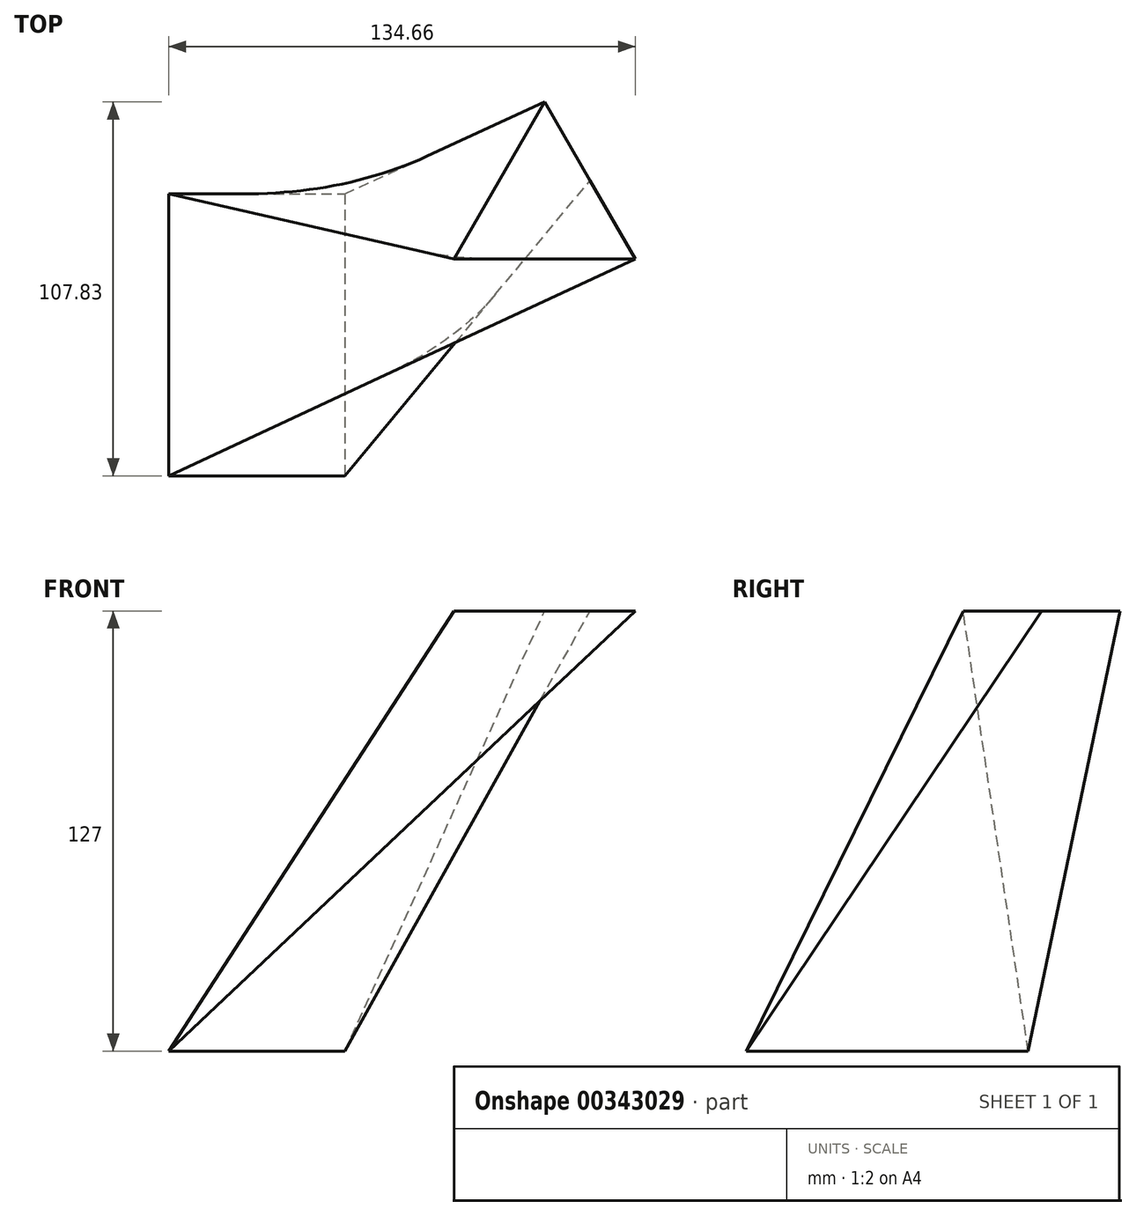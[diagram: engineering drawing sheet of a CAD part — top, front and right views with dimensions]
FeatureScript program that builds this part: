
annotation { "Feature Type Name" : "Feature", "Feature Type Description" : "" }
export const myFeature = defineFeature(function(context is Context, id is Id, definition is map)
    precondition{}
    {
        {
            var Q0;
            Q0=qCreatedBy(makeId("Top.planeOp"),FACE);
            cPlane(context, id + "F0", {"entities" : qUnion([Q0]), "cplaneType" : CPlaneType.OFFSET, "offset" : 127 * mm, "width" : 152.4 * mm, "height" : 152.4 * mm});
        }
        {
            var Q0;
            Q0=qCreatedBy(makeId("Top.planeOp"),FACE);
            var sketch = newSketch(context, id + "F1", { "sketchPlane" : qUnion([Q0])});
            skLineSegment(sketch, "E0.bottom", {"start": v(-65.34, 34.12) * mm, "end": v(-14.52, 34.12) * mm});
            skLineSegment(sketch, "E0.top", {"start": v(-65.34, -47.2) * mm, "end": v(-14.52, -47.2) * mm});
            skLineSegment(sketch, "E0.left", {"start": v(-65.34, 34.12) * mm, "end": v(-65.34, -47.2) * mm});
            skLineSegment(sketch, "E0.right", {"start": v(-14.52, 34.12) * mm, "end": v(-14.52, -47.2) * mm});
            skSolve(sketch);
        }
        {
            var Q0;
            Q0=qCreatedBy(id+"F0.planeOp",FACE);
            var sketch = newSketch(context, id + "F2", { "sketchPlane" : qUnion([Q0])});
            skLineSegment(sketch, "E1", {"start": v(43.18, 60.64) * mm, "end": v(17.04, 15.36) * mm});
            skLineSegment(sketch, "E2", {"start": v(17.04, 15.36) * mm, "end": v(69.32, 15.36) * mm});
            skLineSegment(sketch, "E3", {"start": v(69.32, 15.36) * mm, "end": v(43.18, 60.64) * mm});
            skSolve(sketch);
        }
        {
            var Q0;
            Q0 = qSketchRegion(id + "F1", true);
            var Q1;
            Q1 = qSketchRegion(id + "F2", true);
            loft(context, id + "F3", {"sheetProfilesArray" : [{ "sheetProfileEntities" : qUnion([Q0]) }, { "sheetProfileEntities" : qUnion([Q1]) }]});
        }
    });
